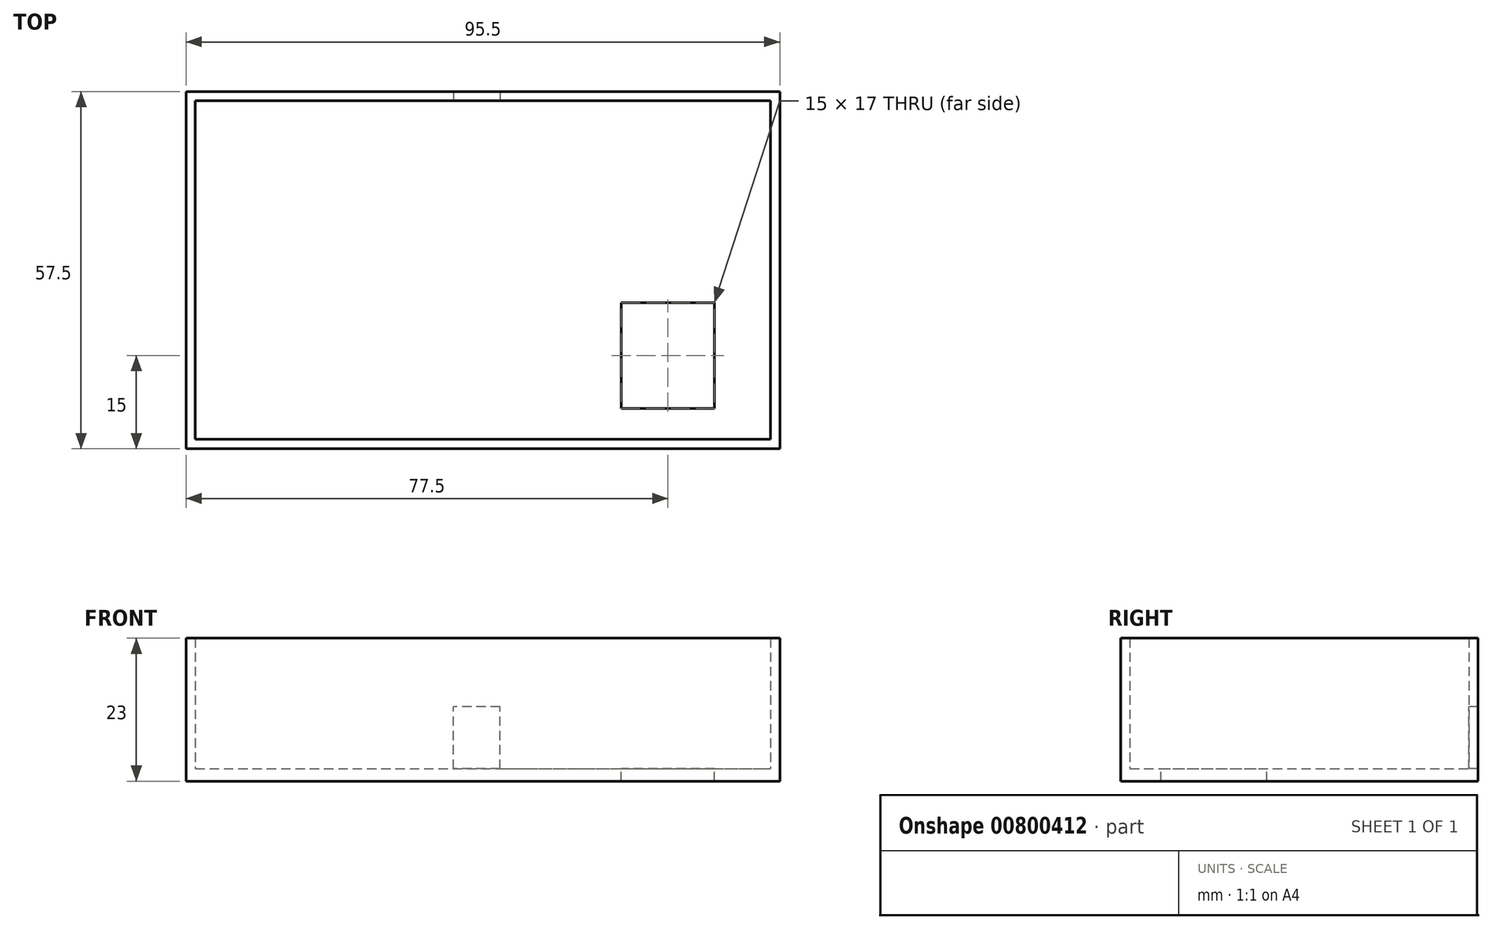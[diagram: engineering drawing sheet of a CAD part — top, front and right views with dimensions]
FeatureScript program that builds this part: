
annotation { "Feature Type Name" : "Feature", "Feature Type Description" : "" }
export const myFeature = defineFeature(function(context is Context, id is Id, definition is map)
    precondition{}
    {
        {
            var Q0;
            Q0=qCreatedBy(makeId("Top.planeOp"),FACE);
            var sketch = newSketch(context, id + "F0", { "sketchPlane" : qUnion([Q0])});
            skLineSegment(sketch, "E0.bottom", {"start": v(0, 0) * mm, "end": v(92.5, 0) * mm});
            skLineSegment(sketch, "E0.top", {"start": v(0, -54.5) * mm, "end": v(92.5, -54.5) * mm});
            skLineSegment(sketch, "E0.left", {"start": v(0, 0) * mm, "end": v(0, -54.5) * mm});
            skLineSegment(sketch, "E0.right", {"start": v(92.5, 0) * mm, "end": v(92.5, -54.5) * mm});
            skLineSegment(sketch, "E1.bottom", {"start": v(-1.5, 1.5) * mm, "end": v(94, 1.5) * mm});
            skLineSegment(sketch, "E1.top", {"start": v(-1.5, -56) * mm, "end": v(94, -56) * mm});
            skLineSegment(sketch, "E1.left", {"start": v(-1.5, 1.5) * mm, "end": v(-1.5, -56) * mm});
            skLineSegment(sketch, "E1.right", {"start": v(94, 1.5) * mm, "end": v(94, -56) * mm});
            skLineSegment(sketch, "E2.bottom", {"start": v(1, -1) * mm, "end": v(91.5, -1) * mm});
            skLineSegment(sketch, "E2.top", {"start": v(1, -53.5) * mm, "end": v(91.5, -53.5) * mm});
            skLineSegment(sketch, "E2.left", {"start": v(1, -1) * mm, "end": v(1, -53.5) * mm});
            skLineSegment(sketch, "E2.right", {"start": v(91.5, -1) * mm, "end": v(91.5, -53.5) * mm});
            skSolve(sketch);
        }
        {
            var Q0;
            Q0=makeQuery(id+"F0.imprint","IMPRINT",FACE,{"disambiguationData":[TD([[makeQuery(id+"F0.imprint","IMPRINT",EDGE,{"derivedFrom":sQuery(id+"F0.wireOp",EDGE,"E0.bottom")}),1.0]])]});
            var Q1;
            Q1=makeQuery(id+"F0.imprint","IMPRINT",FACE,{"disambiguationData":[TD([[makeQuery(id+"F0.imprint","IMPRINT",EDGE,{"derivedFrom":sQuery(id+"F0.wireOp",EDGE,"E0.bottom")}),-1.0]])]});
            var Q2;
            Q2=makeQuery(id+"F0.imprint","IMPRINT",FACE,{"disambiguationData":[TD([[makeQuery(id+"F0.imprint","IMPRINT",EDGE,{"derivedFrom":sQuery(id+"F0.wireOp",EDGE,"E2.bottom")}),-1.0]])]});
            extrude(context, id + "F1", {"entities" : qUnion([Q0, Q1, Q2]), "depth" : 2 * mm, "offsetDistance" : 25 * mm});
        }
        {
            var Q0;
            Q0=makeQuery(id+"F0.imprint","IMPRINT",FACE,{"disambiguationData":[TD([[makeQuery(id+"F0.imprint","IMPRINT",EDGE,{"derivedFrom":sQuery(id+"F0.wireOp",EDGE,"E0.bottom")}),1.0]])]});
            extrude(context, id + "F2", {"entities" : qUnion([Q0]), "operationType" : NewBodyOperationType.ADD, "oppositeDirection" : true, "depth" : 21 * mm, "offsetDistance" : 25 * mm});
        }
        {
            var Q0;
            Q0=makeQuery(id+"F2.opExtrude","SWEPT_FACE",FACE,{"disambiguationData":[OSD([sQuery(id+"F0.wireOp",EDGE,"E0.top")])]});
            var sketch = newSketch(context, id + "F3", { "sketchPlane" : qUnion([Q0])});
            skLineSegment(sketch, "E3.bottom", {"start": v(-49, 0) * mm, "end": v(-41.5, 0) * mm});
            skLineSegment(sketch, "E3.top", {"start": v(-49, -10) * mm, "end": v(-41.5, -10) * mm});
            skLineSegment(sketch, "E3.left", {"start": v(-49, 0) * mm, "end": v(-49, -10) * mm});
            skLineSegment(sketch, "E3.right", {"start": v(-41.5, 0) * mm, "end": v(-41.5, -10) * mm});
            skSolve(sketch);
        }
        {
            var Q0;
            Q0=makeQuery(id+"F3.imprint","IMPRINT",FACE,{"disambiguationData":[TD([[makeQuery(id+"F3.imprint","IMPRINT",EDGE,{"derivedFrom":sQuery(id+"F3.wireOp",EDGE,"E3.bottom")}),1.0]])]});
            extrude(context, id + "F4", {"entities" : qUnion([Q0]), "operationType" : NewBodyOperationType.REMOVE, "endBound" : BoundingType.UP_TO_NEXT, "oppositeDirection" : true, "depth" : 25 * mm, "offsetDistance" : 25 * mm});
        }
        {
            var Q0;
            Q0=makeQuery(id+"F4.boolean.opBoolean","MERGE",FACE,{"derivedFrom":[makeQuery(id+"F1.opExtrude","CAP_FACE",FACE,{"disambiguationData":[OSD([sQuery(id+"F0.wireOp",EDGE,"E1.bottom"),sQuery(id+"F0.wireOp",EDGE,"E1.top"),sQuery(id+"F0.wireOp",EDGE,"E1.left"),sQuery(id+"F0.wireOp",EDGE,"E1.right")])],"isStart":true}),makeQuery(id+"F4.opExtrude","SWEPT_FACE",FACE,{"disambiguationData":[OSD([sQuery(id+"F3.wireOp",EDGE,"E3.bottom")])]})]});
            var sketch = newSketch(context, id + "F5", { "sketchPlane" : qUnion([Q0])});
            skLineSegment(sketch, "E4.bottom", {"start": v(83.5, 5) * mm, "end": v(68.5, 5) * mm});
            skLineSegment(sketch, "E4.top", {"start": v(83.5, 22) * mm, "end": v(68.5, 22) * mm});
            skLineSegment(sketch, "E4.left", {"start": v(83.5, 5) * mm, "end": v(83.5, 22) * mm});
            skLineSegment(sketch, "E4.right", {"start": v(68.5, 5) * mm, "end": v(68.5, 22) * mm});
            skSolve(sketch);
        }
        {
            var Q0;
            Q0 = qSketchRegion(id + "F5", true);
            extrude(context, id + "F6", {"entities" : qUnion([Q0]), "operationType" : NewBodyOperationType.REMOVE, "endBound" : BoundingType.UP_TO_NEXT, "oppositeDirection" : true, "depth" : 25 * mm, "offsetDistance" : 25 * mm});
        }
        {
            var Q0;
            Q0=makeQuery(id+"F1.opExtrude","SWEPT_BODY",BODY,{"disambiguationData":[OSD([sQuery(id+"F0.wireOp",EDGE,"E1.bottom"),sQuery(id+"F0.wireOp",EDGE,"E1.top"),sQuery(id+"F0.wireOp",EDGE,"E1.left"),sQuery(id+"F0.wireOp",EDGE,"E1.right")])]});
            var Q1;
            Q1=makeQuery(id+"F2.opExtrude","CAP_EDGE",EDGE,{"disambiguationData":[OSD([sQuery(id+"F0.wireOp",EDGE,"E1.bottom")])],"isStart":false});
            transform(context, id + "F7", {"entities" : qUnion([Q0]), "transformType" : TransformType.ROTATION, "transformAxis" : qUnion([Q1]), "angle" : 180 * degree, "makeCopy" : false});
        }
    });
